# Revit family: НЕВАТОМ_Шумоглушитель  ГТК, Версия 2
name_source: partatom
category: Арматура воздуховодов
revit_build: Autodesk Revit 2017 (Build: 20170118_1100(x64)
units: mm (PartAtom-declared; Revit-internal decimal feet)

## family parameters
Всегда вертикально = Да
На основе рабочей плоскости = Нет
Общий = Нет
При загрузке вырезать с полостями = Нет
Размер круглого соединителя = Использовать диаметр
Тип детали = Вставляется

## types (18) — shared parameters
ADSK_Единица измерения = шт.
ADSK_Завод-изготовитель = НЕВАТОМ
ADSK_Материал наименование = Оцинкованная сталь
ADSK_Наименование = Глушитель ГТК
ADSK_Потеря давления воздуха = 0.0 Па
Nevatom_URL = https://t.me
Ключевая пометка = Вентиляция
Материал = Сталь оцинкованная
Толщина металла корпуса = 1 мм

## per-type parameters (varying)
| type | ADSK_Количество | ADSK_Размер_Высота | ADSK_Размер_Длина | ADSK_Размер_Ширина | D | D1 | L | d2 |
| ГТК 100-600 | 0 | 200 мм | 200 мм | 600 мм | 100 мм | 200 мм | 600 мм | 220 мм |
| ГТК 100-900 | 0 | 200 мм | 200 мм | 900 мм | 100 мм | 200 мм | 900 мм | 220 мм |
| ГТК 125-600 | 0 | 250 мм | 250 мм | 600 мм | 125 мм | 250 мм | 600 мм | 270 мм |
| ГТК 125-900 | 0 | 250 мм | 250 мм | 900 мм | 125 мм | 250 мм | 900 мм | 270 мм |
| ГТК 160-600 | 1 | 250 мм | 250 мм | 600 мм | 160 мм | 250 мм | 600 мм | 270 мм |
| ГТК 160-900 | 0 | 250 мм | 250 мм | 900 мм | 160 мм | 250 мм | 900 мм | 270 мм |
| ГТК 200-600 | 0 | 315 мм | 315 мм | 600 мм | 200 мм | 315 мм | 600 мм | 335 мм |
| ГТК 200-900 | 0 | 315 мм | 315 мм | 900 мм | 200 мм | 315 мм | 900 мм | 335 мм |
| ГТК 250-600 | 0 | 355 мм | 355 мм | 600 мм | 250 мм | 355 мм | 600 мм | 375 мм |
| ГТК 250-900 | 0 | 355 мм | 355 мм | 900 мм | 250 мм | 355 мм | 900 мм | 375 мм |
| ГТК 315-600 | 0 | 450 мм | 450 мм | 600 мм | 315 мм | 450 мм | 600 мм | 470 мм |
| ГТК 315-900 | 1 | 450 мм | 450 мм | 900 мм | 315 мм | 450 мм | 900 мм | 470 мм |
| ГТК 355-600 | 0 | 500 мм | 500 мм | 600 мм | 355 мм | 500 мм | 600 мм | 520 мм |
| ГТК 355-900 | 0 | 500 мм | 500 мм | 900 мм | 355 мм | 500 мм | 900 мм | 520 мм |
| ГТК 400-600 | 0 | 580 мм | 580 мм | 600 мм | 400 мм | 580 мм | 600 мм | 600 мм |
| ГТК 400-900 | 0 | 580 мм | 580 мм | 900 мм | 400 мм | 580 мм | 900 мм | 600 мм |
| ГТК 500-900 | 0 | 680 мм | 680 мм | 900 мм | 500 мм | 680 мм | 900 мм | 700 мм |
| ГТК 630-900 | 1 | 810 мм | 810 мм | 900 мм | 630 мм | 810 мм | 900 мм | 830 мм |

note: column(s) folded — value = type name in every type: ADSK_Марка
